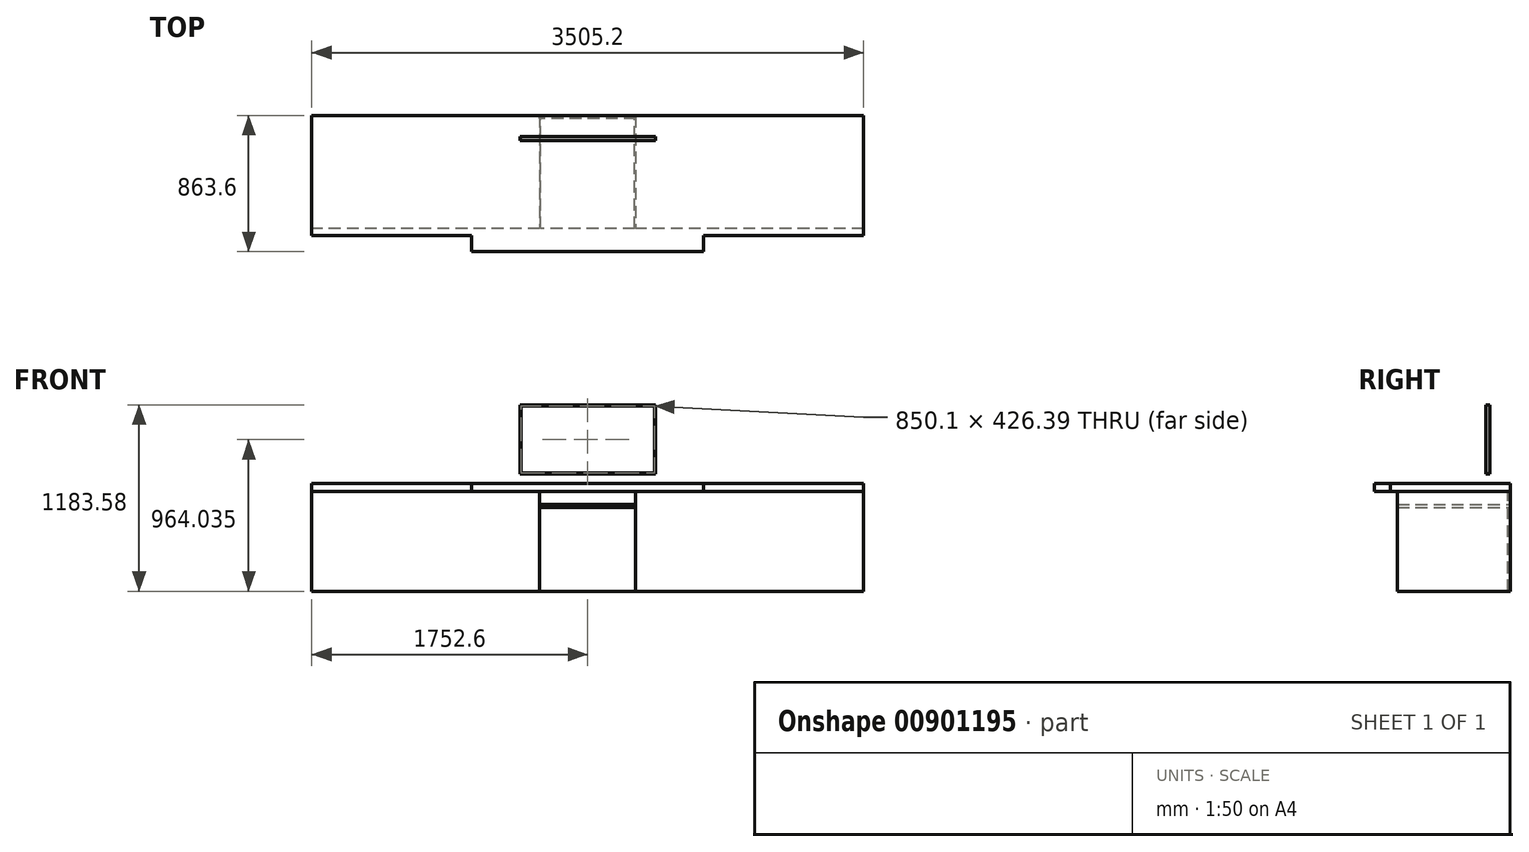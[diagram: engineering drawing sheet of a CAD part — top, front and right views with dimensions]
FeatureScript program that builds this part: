
annotation { "Feature Type Name" : "Feature", "Feature Type Description" : "" }
export const myFeature = defineFeature(function(context is Context, id is Id, definition is map)
    precondition{}
    {
        {
            var Q0;
            Q0=qCreatedBy(makeId("Front.planeOp"),FACE);
            var sketch = newSketch(context, id + "F0", { "sketchPlane" : qUnion([Q0])});
            skLineSegment(sketch, "E0.bottom", {"start": v(1752.6, 127) * mm, "end": v(-1752.6, 127) * mm});
            skLineSegment(sketch, "E0.top", {"start": v(1752.6, 812.8) * mm, "end": v(-1752.6, 812.8) * mm});
            skLineSegment(sketch, "E0.left", {"start": v(1752.6, 127) * mm, "end": v(1752.6, 812.8) * mm});
            skLineSegment(sketch, "E0.right", {"start": v(-1752.6, 127) * mm, "end": v(-1752.6, 812.8) * mm});
            skPoint(sketch, "E0.middle", {"position": v(0, 469.9) * mm});
            skLineSegment(sketch, "E1.bottom", {"start": v(1752.6, 127) * mm, "end": v(1676.4, 127) * mm, "construction": true});
            skLineSegment(sketch, "E1.top", {"start": v(1752.6, 0) * mm, "end": v(1676.4, 0) * mm, "construction": true});
            skLineSegment(sketch, "E1.left", {"start": v(1752.6, 127) * mm, "end": v(1752.6, 0) * mm, "construction": true});
            skLineSegment(sketch, "E1.right", {"start": v(1676.4, 127) * mm, "end": v(1676.4, 0) * mm, "construction": true});
            skLineSegment(sketch, "E2.bottom", {"start": v(-1752.6, 127) * mm, "end": v(-1676.4, 127) * mm, "construction": true});
            skLineSegment(sketch, "E2.top", {"start": v(-1752.6, 0) * mm, "end": v(-1676.4, 0) * mm, "construction": true});
            skLineSegment(sketch, "E2.left", {"start": v(-1752.6, 127) * mm, "end": v(-1752.6, 0) * mm, "construction": true});
            skLineSegment(sketch, "E2.right", {"start": v(-1676.4, 127) * mm, "end": v(-1676.4, 0) * mm, "construction": true});
            skSolve(sketch);
        }
        {
            var Q0;
            Q0 = qSketchRegion(id + "F0", true);
            var Q1;
            Q1 = qConstructionFilter(qBodyType(qCreatedBy(id + "F0" ,EDGE), BodyType.WIRE), ConstructionObject.NO);
            extrude(context, id + "F1", {"entities" : qUnion([Q0]), "surfaceEntities" : qUnion([Q1]), "endBound" : BoundingType.SYMMETRIC, "depth" : 762 * mm, "offsetDistance" : 25.4 * mm});
        }
        {
            var Q0;
            Q0=makeQuery(id+"F1.opExtrude","CAP_FACE",FACE,{"disambiguationData":[OSD([sQuery(id+"F0.wireOp",EDGE,"E0.bottom"),sQuery(id+"F0.wireOp",EDGE,"E0.top"),sQuery(id+"F0.wireOp",EDGE,"E0.left"),sQuery(id+"F0.wireOp",EDGE,"E0.right")])],"isStart":false});
            var sketch = newSketch(context, id + "F2", { "sketchPlane" : qUnion([Q0])});
            skLineSegment(sketch, "E3.bottom", {"start": v(304.8, 127) * mm, "end": v(-304.8, 127) * mm});
            skLineSegment(sketch, "E3.top", {"start": v(304.8, 762) * mm, "end": v(-304.8, 762) * mm});
            skLineSegment(sketch, "E3.left", {"start": v(304.8, 127) * mm, "end": v(304.8, 762) * mm});
            skLineSegment(sketch, "E3.right", {"start": v(-304.8, 127) * mm, "end": v(-304.8, 762) * mm});
            skPoint(sketch, "E3.middle", {"position": v(0, 444.5) * mm});
            skPoint(sketch, "E3.middle.positionSnap0", {"position": v(0, 127) * mm});
            skPoint(sketch, "E3.centerSnap0", {"position": v(0, 127) * mm});
            skSolve(sketch);
        }
        {
            var Q0;
            Q0 = qSketchRegion(id + "F2", true);
            extrude(context, id + "F3", {"entities" : qUnion([Q0]), "operationType" : NewBodyOperationType.REMOVE, "oppositeDirection" : true, "depth" : 843.28 * mm, "offsetDistance" : 25.4 * mm});
        }
        {
            var Q0;
            Q0=qCreatedBy(makeId("Top.planeOp"),FACE);
            cPlane(context, id + "F4", {"entities" : qUnion([Q0]), "cplaneType" : CPlaneType.OFFSET, "offset" : 660.4 * mm, "width" : 152.4 * mm, "height" : 152.4 * mm});
        }
        {
            var Q0;
            Q0=qCreatedBy(id+"F4.planeOp",FACE);
            var sketch = newSketch(context, id + "F5", { "sketchPlane" : qUnion([Q0])});
            skLineSegment(sketch, "E4.bottom", {"start": v(304.8, -381) * mm, "end": v(-304.8, -381) * mm, "construction": true});
            skLineSegment(sketch, "E4.top", {"start": v(304.8, 381) * mm, "end": v(-304.8, 381) * mm, "construction": true});
            skLineSegment(sketch, "E4.left", {"start": v(304.8, -381) * mm, "end": v(304.8, 381) * mm, "construction": true});
            skLineSegment(sketch, "E4.right", {"start": v(-304.8, -381) * mm, "end": v(-304.8, 381) * mm, "construction": true});
            skPoint(sketch, "E4.middle", {"position": v(0, 0) * mm});
            skLineSegment(sketch, "E5.bottom", {"start": v(-298.45, -381) * mm, "end": v(298.45, -381) * mm});
            skLineSegment(sketch, "E5.top", {"start": v(-298.45, 381) * mm, "end": v(298.45, 381) * mm});
            skLineSegment(sketch, "E5.left", {"start": v(-298.45, -381) * mm, "end": v(-298.45, 381) * mm});
            skLineSegment(sketch, "E5.right", {"start": v(298.45, -381) * mm, "end": v(298.45, 381) * mm});
            skSolve(sketch);
        }
        {
            var Q0;
            Q0 = qSketchRegion(id + "F5", true);
            extrude(context, id + "F6", {"entities" : qUnion([Q0]), "depth" : 19.05 * mm, "offsetDistance" : 25.4 * mm});
        }
        {
            var Q0;
            Q0=makeQuery(id+"F1.opExtrude","SWEPT_FACE",FACE,{"disambiguationData":[OSD([sQuery(id+"F0.wireOp",EDGE,"E0.top")])]});
            extrude(context, id + "F7", {"entities" : qUnion([Q0]), "operationType" : NewBodyOperationType.REMOVE, "oppositeDirection" : true, "depth" : 50.8 * mm, "offsetDistance" : 25.4 * mm});
        }
        {
            var Q0;
            {var subQ0=sQuery(id+"F0.wireOp",EDGE,"E0.right");var subQ2=sQuery(id+"F0.wireOp",EDGE,"E0.top");Q0=makeQuery(id+"F7.boolean.opBoolean","COPY",FACE,{"disambiguationData":[TD([makeQuery(id+"F1.opExtrude","SWEPT_FACE",FACE,{"disambiguationData":[OSD([subQ0])]})])],"derivedFrom":makeQuery(id+"F7.opExtrude","CAP_FACE",FACE,{"disambiguationData":[OSD([subQ2])],"isStart":false})});}
            var sketch = newSketch(context, id + "F8", { "sketchPlane" : qUnion([Q0])});
            skLineSegment(sketch, "E6.bottom", {"start": v(-1752.6, 381) * mm, "end": v(1752.6, 381) * mm});
            skLineSegment(sketch, "E6.top", {"start": v(-1752.6, -381) * mm, "end": v(1752.6, -381) * mm});
            skLineSegment(sketch, "E6.left", {"start": v(-1752.6, 381) * mm, "end": v(-1752.6, -381) * mm});
            skLineSegment(sketch, "E6.right", {"start": v(1752.6, 381) * mm, "end": v(1752.6, -381) * mm});
            skLineSegment(sketch, "E7.bottom", {"start": v(736.6, -381) * mm, "end": v(-736.6, -381) * mm});
            skLineSegment(sketch, "E7.top", {"start": v(736.6, -482.6) * mm, "end": v(-736.6, -482.6) * mm});
            skLineSegment(sketch, "E7.left", {"start": v(736.6, -381) * mm, "end": v(736.6, -482.6) * mm});
            skLineSegment(sketch, "E7.right", {"start": v(-736.6, -381) * mm, "end": v(-736.6, -482.6) * mm});
            skPoint(sketch, "E7.middle", {"position": v(0, -431.8) * mm});
            skPoint(sketch, "E7.middle.positionSnap0", {"position": v(0, -381) * mm});
            skPoint(sketch, "E7.centerSnap0", {"position": v(0, -381) * mm});
            skSolve(sketch);
        }
        {
            var Q0;
            Q0 = qSketchRegion(id + "F8", true);
            extrude(context, id + "F9", {"entities" : qUnion([Q0]), "depth" : 50.8 * mm, "offsetDistance" : 25.4 * mm});
        }
        {
            var Q0;
            {var subQ0=sQuery(id+"F0.wireOp",EDGE,"E0.bottom");var subQ1=sQuery(id+"F0.wireOp",EDGE,"E0.right");var subQ2=sQuery(id+"F0.wireOp",EDGE,"E0.top");Q0=makeQuery(id+"F7.boolean.opBoolean","SPLIT",FACE,{"disambiguationData":[TD([makeQuery(id+"F1.opExtrude","SWEPT_FACE",FACE,{"disambiguationData":[OSD([subQ1])]})])],"derivedFrom":makeQuery(id+"F1.opExtrude","CAP_FACE",FACE,{"disambiguationData":[OSD([subQ0,subQ2,sQuery(id+"F0.wireOp",EDGE,"E0.left"),subQ1])],"isStart":false})});}
            var Q1;
            {var subQ0=sQuery(id+"F0.wireOp",EDGE,"E0.bottom");var subQ1=sQuery(id+"F0.wireOp",EDGE,"E0.left");var subQ2=sQuery(id+"F0.wireOp",EDGE,"E0.top");Q1=makeQuery(id+"F7.boolean.opBoolean","SPLIT",FACE,{"disambiguationData":[TD([makeQuery(id+"F1.opExtrude","SWEPT_FACE",FACE,{"disambiguationData":[OSD([subQ1])]})])],"derivedFrom":makeQuery(id+"F1.opExtrude","CAP_FACE",FACE,{"disambiguationData":[OSD([subQ0,subQ2,subQ1,sQuery(id+"F0.wireOp",EDGE,"E0.right")])],"isStart":false})});}
            var Q2;
            Q2=makeQuery(id+"F6.opExtrude","SWEPT_FACE",FACE,{"disambiguationData":[OSD([sQuery(id+"F5.wireOp",EDGE,"E5.bottom")])]});
            extrude(context, id + "F10", {"entities" : qUnion([Q0, Q1, Q2]), "operationType" : NewBodyOperationType.REMOVE, "oppositeDirection" : true, "depth" : 25.4 * mm, "offsetDistance" : 25.4 * mm});
        }
        {
            var Q0;
            {var subQ0=sQuery(id+"F0.wireOp",EDGE,"E0.bottom");var subQ1=sQuery(id+"F0.wireOp",EDGE,"E0.right");var subQ2=sQuery(id+"F0.wireOp",EDGE,"E0.top");var subQ3=sQuery(id+"F0.wireOp",EDGE,"E0.left");Q0=makeQuery(id+"F10.boolean.opBoolean","COPY",FACE,{"derivedFrom":makeQuery(id+"F10.opExtrude","CAP_FACE",FACE,{"disambiguationData":[OSD([subQ0,subQ2,subQ3,subQ1]),TDD([makeQuery(id+"F7.boolean.opBoolean","SPLIT",FACE,{"disambiguationData":[TD([makeQuery(id+"F1.opExtrude","SWEPT_FACE",FACE,{"disambiguationData":[OSD([subQ1])]})])],"derivedFrom":makeQuery(id+"F1.opExtrude","CAP_FACE",FACE,{"disambiguationData":[OSD([subQ0,subQ2,subQ3,subQ1])],"isStart":false})})])],"isStart":false})});}
            var sketch = newSketch(context, id + "F11", { "sketchPlane" : qUnion([Q0])});
            skLineSegment(sketch, "E8.bottom", {"start": v(-739.78, 758.82) * mm, "end": v(-1749.42, 758.82) * mm});
            skLineSegment(sketch, "E8.top", {"start": v(-739.78, 631.83) * mm, "end": v(-1749.42, 631.82) * mm});
            skLineSegment(sketch, "E8.left", {"start": v(-739.78, 758.82) * mm, "end": v(-739.78, 631.82) * mm});
            skLineSegment(sketch, "E8.right", {"start": v(-1749.42, 758.82) * mm, "end": v(-1749.42, 631.82) * mm});
            skPoint(sketch, "E8.middle", {"position": v(-1244.6, 695.32) * mm});
            skPoint(sketch, "E8.middle.positionSnap0", {"position": v(-1244.6, 738.9) * mm});
            skLineSegment(sketch, "E9.bottom", {"start": v(-739.78, 628.65) * mm, "end": v(-1749.42, 628.65) * mm});
            skLineSegment(sketch, "E9.top", {"start": v(-739.78, 412.75) * mm, "end": v(-1749.42, 412.75) * mm});
            skLineSegment(sketch, "E9.left", {"start": v(-739.78, 628.65) * mm, "end": v(-739.78, 412.75) * mm});
            skLineSegment(sketch, "E9.right", {"start": v(-1749.42, 628.65) * mm, "end": v(-1749.42, 412.75) * mm});
            skPoint(sketch, "E9.middle", {"position": v(-1244.6, 520.7) * mm});
            skLineSegment(sketch, "E10.bottom", {"start": v(-739.78, 409.57) * mm, "end": v(-1749.42, 409.57) * mm});
            skLineSegment(sketch, "E10.top", {"start": v(-739.78, 130.18) * mm, "end": v(-1749.42, 130.18) * mm});
            skLineSegment(sketch, "E10.left", {"start": v(-739.78, 409.57) * mm, "end": v(-739.78, 130.18) * mm});
            skLineSegment(sketch, "E10.right", {"start": v(-1749.42, 409.57) * mm, "end": v(-1749.42, 130.18) * mm});
            skPoint(sketch, "E10.middle", {"position": v(-1244.6, 269.88) * mm});
            skPoint(sketch, "E10.middle.positionSnap0", {"position": v(-1244.6, 412.75) * mm});
            skPoint(sketch, "E10.centerSnap0", {"position": v(-1244.6, 412.75) * mm});
            skLineSegment(sketch, "E11", {"start": v(-1749.42, 758.82) * mm, "end": v(-1749.42, 762) * mm, "construction": true});
            skLineSegment(sketch, "E12", {"start": v(-1749.42, 631.82) * mm, "end": v(-1749.42, 628.65) * mm, "construction": true});
            skLineSegment(sketch, "E13", {"start": v(-1749.42, 412.75) * mm, "end": v(-1749.42, 409.57) * mm, "construction": true});
            skLineSegment(sketch, "E14", {"start": v(-1749.42, 758.82) * mm, "end": v(-1752.6, 758.82) * mm, "construction": true});
            skLineSegment(sketch, "E15", {"start": v(-1749.42, 130.18) * mm, "end": v(-1749.42, 127) * mm, "construction": true});
            skLineSegment(sketch, "E16.MirrorCS", {"start": v(1749.42, 758.83) * mm, "end": v(1752.6, 758.83) * mm, "construction": true});
            skLineSegment(sketch, "E17.MirrorCS", {"start": v(1749.42, 758.82) * mm, "end": v(1749.42, 762) * mm, "construction": true});
            skLineSegment(sketch, "E18.MirrorCS", {"start": v(1749.42, 631.82) * mm, "end": v(1749.42, 628.65) * mm, "construction": true});
            skLineSegment(sketch, "E19.MirrorCS", {"start": v(1749.42, 412.75) * mm, "end": v(1749.42, 409.57) * mm, "construction": true});
            skLineSegment(sketch, "E20.MirrorCS", {"start": v(1749.42, 130.18) * mm, "end": v(1749.42, 127) * mm, "construction": true});
            skPoint(sketch, "E21.MirrorP", {"position": v(1244.6, 412.75) * mm});
            skPoint(sketch, "E22.MirrorP", {"position": v(1244.6, 594.57) * mm});
            skPoint(sketch, "E23.MirrorP", {"position": v(1244.6, 695.32) * mm});
            skLineSegment(sketch, "E24.MirrorCS", {"start": v(739.78, 130.18) * mm, "end": v(1749.42, 130.18) * mm});
            skLineSegment(sketch, "E25.MirrorCS", {"start": v(739.78, 409.57) * mm, "end": v(739.78, 130.18) * mm});
            skLineSegment(sketch, "E26.MirrorCS", {"start": v(739.78, 758.83) * mm, "end": v(1749.42, 758.83) * mm});
            skLineSegment(sketch, "E27.MirrorCS", {"start": v(739.78, 409.57) * mm, "end": v(1749.42, 409.58) * mm});
            skLineSegment(sketch, "E28.MirrorCS", {"start": v(1749.42, 409.57) * mm, "end": v(1749.42, 130.18) * mm});
            skLineSegment(sketch, "E29.MirrorCS", {"start": v(1749.42, 758.82) * mm, "end": v(1749.42, 631.82) * mm});
            skPoint(sketch, "E30.MirrorP", {"position": v(1244.6, 738.9) * mm});
            skLineSegment(sketch, "E31.MirrorCS", {"start": v(739.78, 412.75) * mm, "end": v(1749.42, 412.75) * mm});
            skLineSegment(sketch, "E32.MirrorCS", {"start": v(739.78, 631.83) * mm, "end": v(1749.42, 631.83) * mm});
            skPoint(sketch, "E33.MirrorP", {"position": v(1244.6, 269.88) * mm});
            skLineSegment(sketch, "E34.MirrorCS", {"start": v(739.78, 628.65) * mm, "end": v(1749.42, 628.65) * mm});
            skPoint(sketch, "E35.MirrorP", {"position": v(1244.6, 520.7) * mm});
            skLineSegment(sketch, "E36.MirrorCS", {"start": v(739.78, 758.82) * mm, "end": v(739.78, 631.82) * mm});
            skLineSegment(sketch, "E37.MirrorCS", {"start": v(739.78, 628.65) * mm, "end": v(739.78, 412.75) * mm});
            skLineSegment(sketch, "E38.MirrorCS", {"start": v(1749.42, 628.65) * mm, "end": v(1749.42, 412.75) * mm});
            skLineSegment(sketch, "E39.bottom", {"start": v(-307.97, 758.82) * mm, "end": v(-736.6, 758.82) * mm});
            skLineSegment(sketch, "E39.top", {"start": v(-307.97, 446.09) * mm, "end": v(-736.6, 446.09) * mm});
            skLineSegment(sketch, "E39.left", {"start": v(-307.97, 758.82) * mm, "end": v(-307.97, 446.09) * mm});
            skLineSegment(sketch, "E39.right", {"start": v(-736.6, 758.82) * mm, "end": v(-736.6, 446.09) * mm});
            skPoint(sketch, "E39.middle", {"position": v(-522.29, 602.46) * mm});
            skLineSegment(sketch, "E40.bottom", {"start": v(-307.97, 442.91) * mm, "end": v(-736.6, 442.91) * mm});
            skLineSegment(sketch, "E40.top", {"start": v(-307.97, 130.18) * mm, "end": v(-736.6, 130.18) * mm});
            skLineSegment(sketch, "E40.left", {"start": v(-307.97, 442.91) * mm, "end": v(-307.97, 130.18) * mm});
            skLineSegment(sketch, "E40.right", {"start": v(-736.6, 442.91) * mm, "end": v(-736.6, 130.18) * mm});
            skPoint(sketch, "E40.middle", {"position": v(-522.29, 286.54) * mm});
            skLineSegment(sketch, "E41", {"start": v(-736.6, 758.82) * mm, "end": v(-739.78, 758.82) * mm, "construction": true});
            skLineSegment(sketch, "E42", {"start": v(-307.97, 758.82) * mm, "end": v(-304.8, 758.82) * mm, "construction": true});
            skLineSegment(sketch, "E43", {"start": v(-736.6, 758.82) * mm, "end": v(-736.6, 762) * mm, "construction": true});
            skLineSegment(sketch, "E44", {"start": v(-736.6, 446.09) * mm, "end": v(-736.6, 442.91) * mm, "construction": true});
            skLineSegment(sketch, "E45", {"start": v(-736.6, 130.18) * mm, "end": v(-736.6, 127) * mm, "construction": true});
            skLineSegment(sketch, "E46.MirrorCS", {"start": v(307.97, 758.82) * mm, "end": v(307.97, 446.09) * mm});
            skLineSegment(sketch, "E47.MirrorCS", {"start": v(307.97, 758.82) * mm, "end": v(736.6, 758.82) * mm});
            skLineSegment(sketch, "E48.MirrorCS", {"start": v(736.6, 758.82) * mm, "end": v(736.6, 446.09) * mm});
            skLineSegment(sketch, "E49.MirrorCS", {"start": v(307.97, 446.09) * mm, "end": v(736.6, 446.09) * mm});
            skLineSegment(sketch, "E50.MirrorCS", {"start": v(307.97, 442.91) * mm, "end": v(307.97, 130.18) * mm});
            skLineSegment(sketch, "E51.MirrorCS", {"start": v(736.6, 442.91) * mm, "end": v(736.6, 130.18) * mm});
            skLineSegment(sketch, "E52.MirrorCS", {"start": v(307.97, 130.18) * mm, "end": v(736.6, 130.18) * mm});
            skLineSegment(sketch, "E53.MirrorCS", {"start": v(307.97, 442.91) * mm, "end": v(736.6, 442.91) * mm});
            skLineSegment(sketch, "E54.bottom", {"start": v(-1752.6, 762) * mm, "end": v(-304.8, 762) * mm, "construction": true});
            skLineSegment(sketch, "E54.top", {"start": v(-1752.6, 127) * mm, "end": v(-304.8, 127) * mm, "construction": true});
            skLineSegment(sketch, "E54.left", {"start": v(-1752.6, 762) * mm, "end": v(-1752.6, 127) * mm, "construction": true});
            skLineSegment(sketch, "E54.right", {"start": v(-304.8, 762) * mm, "end": v(-304.8, 127) * mm, "construction": true});
            skPoint(sketch, "E55", {"position": v(-1244.6, 758.82) * mm});
            skSolve(sketch);
        }
        {
            var Q0;
            Q0 = qSketchRegion(id + "F11", true);
            extrude(context, id + "F12", {"entities" : qUnion([Q0]), "oppositeDirection" : true, "depth" : 19.05 * mm, "offsetDistance" : 25.4 * mm});
        }
        {
            var Q0;
            Q0=makeQuery(id+"F12.opExtrude","SWEPT_BODY",BODY,{"disambiguationData":[OSD([sQuery(id+"F11.wireOp",EDGE,"E50.MirrorCS"),sQuery(id+"F11.wireOp",EDGE,"E51.MirrorCS"),sQuery(id+"F11.wireOp",EDGE,"E52.MirrorCS"),sQuery(id+"F11.wireOp",EDGE,"E53.MirrorCS")])]});
            var Q1;
            Q1=makeQuery(id+"F12.opExtrude","SWEPT_BODY",BODY,{"disambiguationData":[OSD([sQuery(id+"F11.wireOp",EDGE,"E8.bottom"),sQuery(id+"F11.wireOp",EDGE,"E8.top"),sQuery(id+"F11.wireOp",EDGE,"E8.left"),sQuery(id+"F11.wireOp",EDGE,"E8.right")])]});
            var Q2;
            Q2=makeQuery(id+"F12.opExtrude","SWEPT_BODY",BODY,{"disambiguationData":[OSD([sQuery(id+"F11.wireOp",EDGE,"E9.bottom"),sQuery(id+"F11.wireOp",EDGE,"E9.top"),sQuery(id+"F11.wireOp",EDGE,"E9.left"),sQuery(id+"F11.wireOp",EDGE,"E9.right")])]});
            var Q3;
            Q3=makeQuery(id+"F12.opExtrude","SWEPT_BODY",BODY,{"disambiguationData":[OSD([sQuery(id+"F11.wireOp",EDGE,"E10.bottom"),sQuery(id+"F11.wireOp",EDGE,"E10.top"),sQuery(id+"F11.wireOp",EDGE,"E10.left"),sQuery(id+"F11.wireOp",EDGE,"E10.right")])]});
            var Q4;
            Q4=makeQuery(id+"F12.opExtrude","SWEPT_BODY",BODY,{"disambiguationData":[OSD([sQuery(id+"F11.wireOp",EDGE,"E24.MirrorCS"),sQuery(id+"F11.wireOp",EDGE,"E25.MirrorCS"),sQuery(id+"F11.wireOp",EDGE,"E27.MirrorCS"),sQuery(id+"F11.wireOp",EDGE,"E28.MirrorCS")])]});
            var Q5;
            Q5=makeQuery(id+"F12.opExtrude","SWEPT_BODY",BODY,{"disambiguationData":[OSD([sQuery(id+"F11.wireOp",EDGE,"E26.MirrorCS"),sQuery(id+"F11.wireOp",EDGE,"E29.MirrorCS"),sQuery(id+"F11.wireOp",EDGE,"E32.MirrorCS"),sQuery(id+"F11.wireOp",EDGE,"E36.MirrorCS")])]});
            var Q6;
            Q6=makeQuery(id+"F12.opExtrude","SWEPT_BODY",BODY,{"disambiguationData":[OSD([sQuery(id+"F11.wireOp",EDGE,"E31.MirrorCS"),sQuery(id+"F11.wireOp",EDGE,"E34.MirrorCS"),sQuery(id+"F11.wireOp",EDGE,"E37.MirrorCS"),sQuery(id+"F11.wireOp",EDGE,"E38.MirrorCS")])]});
            var Q7;
            Q7=makeQuery(id+"F12.opExtrude","SWEPT_BODY",BODY,{"disambiguationData":[OSD([sQuery(id+"F11.wireOp",EDGE,"E39.bottom"),sQuery(id+"F11.wireOp",EDGE,"E39.top"),sQuery(id+"F11.wireOp",EDGE,"E39.left"),sQuery(id+"F11.wireOp",EDGE,"E39.right")])]});
            var Q8;
            Q8=makeQuery(id+"F12.opExtrude","SWEPT_BODY",BODY,{"disambiguationData":[OSD([sQuery(id+"F11.wireOp",EDGE,"E40.bottom"),sQuery(id+"F11.wireOp",EDGE,"E40.top"),sQuery(id+"F11.wireOp",EDGE,"E40.left"),sQuery(id+"F11.wireOp",EDGE,"E40.right")])]});
            var Q9;
            Q9=makeQuery(id+"F12.opExtrude","SWEPT_BODY",BODY,{"disambiguationData":[OSD([sQuery(id+"F11.wireOp",EDGE,"E46.MirrorCS"),sQuery(id+"F11.wireOp",EDGE,"E47.MirrorCS"),sQuery(id+"F11.wireOp",EDGE,"E48.MirrorCS"),sQuery(id+"F11.wireOp",EDGE,"E49.MirrorCS")])]});
            var Q10;
            Q10=makeQuery(id+"F7.boolean.opBoolean","SPLIT",BODY,{"disambiguationData":[OD(1.0)],"derivedFrom":makeQuery(id+"F1.opExtrude","SWEPT_BODY",BODY,{"disambiguationData":[OSD([sQuery(id+"F0.wireOp",EDGE,"E0.bottom"),sQuery(id+"F0.wireOp",EDGE,"E0.top"),sQuery(id+"F0.wireOp",EDGE,"E0.left"),sQuery(id+"F0.wireOp",EDGE,"E0.right")])]})});
            var Q11;
            Q11=makeQuery(id+"F7.boolean.opBoolean","SPLIT",BODY,{"disambiguationData":[OD(0.0)],"derivedFrom":makeQuery(id+"F1.opExtrude","SWEPT_BODY",BODY,{"disambiguationData":[OSD([sQuery(id+"F0.wireOp",EDGE,"E0.bottom"),sQuery(id+"F0.wireOp",EDGE,"E0.top"),sQuery(id+"F0.wireOp",EDGE,"E0.left"),sQuery(id+"F0.wireOp",EDGE,"E0.right")])]})});
            booleanBodies(context, id + "F13", {"operationType" : BooleanOperationType.SUBTRACTION, "tools" : qUnion([Q0, Q1, Q2, Q3, Q4, Q5, Q6, Q7, Q8, Q9]), "targets" : qUnion([Q10, Q11]), "keepTools" : true});
        }
        {
            var Q0;
            Q0=makeQuery(id+"F1.opExtrude","SWEPT_FACE",FACE,{"disambiguationData":[OSD([sQuery(id+"F0.wireOp",EDGE,"E0.right")])]});
            var sketch = newSketch(context, id + "F14", { "sketchPlane" : qUnion([Q0])});
            skLineSegment(sketch, "E56.bottom", {"start": v(336.55, 762) * mm, "end": v(355.6, 762) * mm});
            skLineSegment(sketch, "E56.top", {"start": v(336.55, 127) * mm, "end": v(355.6, 127) * mm});
            skLineSegment(sketch, "E56.left", {"start": v(336.55, 762) * mm, "end": v(336.55, 127) * mm});
            skLineSegment(sketch, "E56.right", {"start": v(355.6, 762) * mm, "end": v(355.6, 127) * mm});
            skSolve(sketch);
        }
        {
            var Q0;
            Q0 = qSketchRegion(id + "F14", true);
            extrude(context, id + "F15", {"entities" : qUnion([Q0]), "operationType" : NewBodyOperationType.REMOVE, "oppositeDirection" : true, "depth" : 4173.22 * mm, "offsetDistance" : 25.4 * mm});
        }
        {
            var Q0;
            Q0=makeQuery(id+"F9.opExtrude","SWEPT_FACE",FACE,{"disambiguationData":[OSD([sQuery(id+"F8.wireOp",EDGE,"E6.bottom")])]});
            cPlane(context, id + "F16", {"entities" : qUnion([Q0]), "cplaneType" : CPlaneType.OFFSET, "offset" : 157.48 * mm, "oppositeDirection" : true, "width" : 152.4 * mm, "height" : 152.4 * mm});
        }
        {
            var Q0;
            Q0=qCreatedBy(id+"F16.planeOp",FACE);
            var sketch = newSketch(context, id + "F17", { "sketchPlane" : qUnion([Q0])});
            skLineSegment(sketch, "E57.bottom", {"start": v(-431.4, 871.49) * mm, "end": v(431.4, 871.49) * mm});
            skLineSegment(sketch, "E57.top", {"start": v(-431.4, 1310.58) * mm, "end": v(431.4, 1310.58) * mm});
            skLineSegment(sketch, "E57.left", {"start": v(-431.4, 871.49) * mm, "end": v(-431.4, 1310.58) * mm});
            skLineSegment(sketch, "E57.right", {"start": v(431.4, 871.49) * mm, "end": v(431.4, 1310.58) * mm});
            skPoint(sketch, "E57.middle", {"position": v(0, 1091.03) * mm});
            skLineSegment(sketch, "E58.0", {"start": v(425.05, 877.84) * mm, "end": v(425.05, 1304.23) * mm});
            skLineSegment(sketch, "E58.1", {"start": v(-425.05, 877.84) * mm, "end": v(425.05, 877.84) * mm});
            skLineSegment(sketch, "E58.2", {"start": v(-425.05, 877.84) * mm, "end": v(-425.05, 1304.23) * mm});
            skLineSegment(sketch, "E58.3", {"start": v(-425.05, 1304.23) * mm, "end": v(425.05, 1304.23) * mm});
            skSolve(sketch);
        }
        {
            var Q0;
            Q0 = qSketchRegion(id + "F17", true);
            extrude(context, id + "F18", {"entities" : qUnion([Q0]), "depth" : 25.4 * mm, "offsetDistance" : 25.4 * mm});
        }
        {
            var Q0;
            Q0=makeQuery(id+"F17.imprint","IMPRINT",FACE,{"disambiguationData":[TD([[makeQuery(id+"F17.imprint","IMPRINT",EDGE,{"derivedFrom":sQuery(id+"F17.wireOp",EDGE,"E58.0")}),1.0]])]});
            extrude(context, id + "F19", {"entities" : qUnion([Q0]), "depth" : 25.4 * mm, "offsetDistance" : 25.4 * mm});
        }
        {
            var Q0;
            {var subQ0=sQuery(id+"F0.wireOp",EDGE,"E0.bottom");var subQ1=sQuery(id+"F0.wireOp",EDGE,"E0.left");var subQ2=sQuery(id+"F0.wireOp",EDGE,"E0.top");Q0=makeQuery(id+"F7.boolean.opBoolean","SPLIT",FACE,{"disambiguationData":[TD([makeQuery(id+"F1.opExtrude","SWEPT_FACE",FACE,{"disambiguationData":[OSD([subQ1])]})])],"derivedFrom":makeQuery(id+"F1.opExtrude","CAP_FACE",FACE,{"disambiguationData":[OSD([subQ0,subQ2,subQ1,sQuery(id+"F0.wireOp",EDGE,"E0.right")])],"isStart":true})});}
            var sketch = newSketch(context, id + "F20", { "sketchPlane" : qUnion([Q0])});
            skLineSegment(sketch, "E59.bottom", {"start": v(-304.8, 762) * mm, "end": v(304.8, 762) * mm});
            skLineSegment(sketch, "E59.top", {"start": v(-304.8, 127) * mm, "end": v(304.8, 127) * mm});
            skLineSegment(sketch, "E59.left", {"start": v(-304.8, 762) * mm, "end": v(-304.8, 127) * mm});
            skLineSegment(sketch, "E59.right", {"start": v(304.8, 762) * mm, "end": v(304.8, 127) * mm});
            skSolve(sketch);
        }
        {
            var Q0;
            Q0 = qSketchRegion(id + "F20", true);
            extrude(context, id + "F21", {"entities" : qUnion([Q0]), "oppositeDirection" : true, "depth" : 17.78 * mm, "offsetDistance" : 25.4 * mm});
        }
    });
